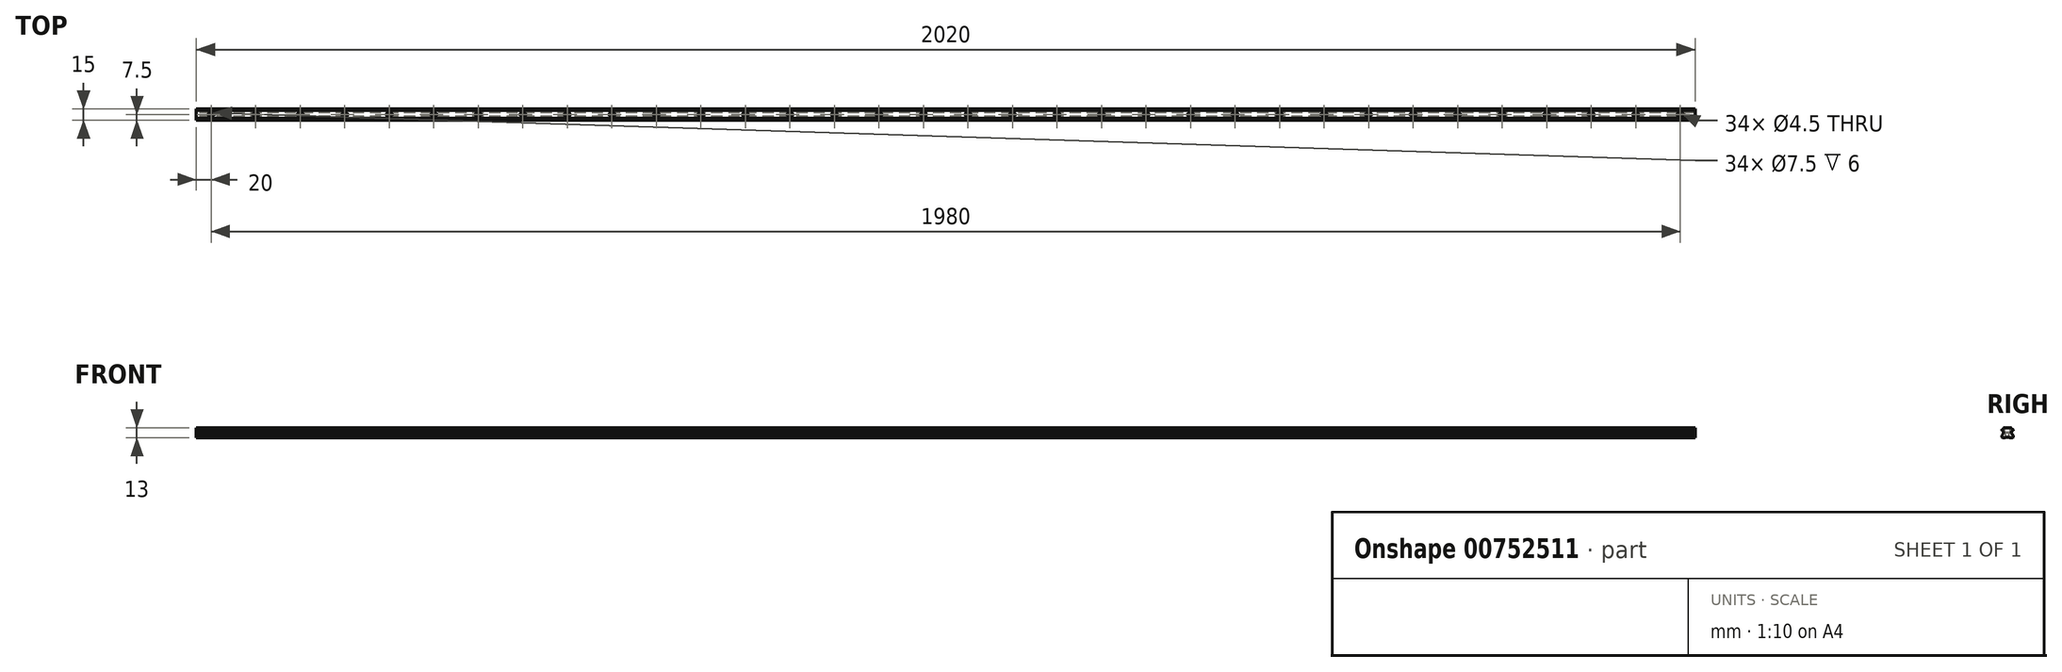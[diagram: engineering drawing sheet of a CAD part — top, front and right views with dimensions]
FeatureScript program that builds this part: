
annotation { "Feature Type Name" : "Feature", "Feature Type Description" : "" }
export const myFeature = defineFeature(function(context is Context, id is Id, definition is map)
    precondition{}
    {
        {
            var Q0;
            Q0=qCreatedBy(makeId("Right.planeOp"),FACE);
            var sketch = newSketch(context, id + "F0", { "sketchPlane" : qUnion([Q0])});
            skLineSegment(sketch, "E0", {"start": v(0, 0.5) * mm, "end": v(2.5, 0.5) * mm});
            skLineSegment(sketch, "E1", {"start": v(2.5, 0.5) * mm, "end": v(3, 0) * mm});
            skLineSegment(sketch, "E2", {"start": v(3, 0) * mm, "end": v(7, 0) * mm});
            skLineSegment(sketch, "E3", {"start": v(7, 0) * mm, "end": v(7.5, 0.5) * mm});
            skLineSegment(sketch, "E4", {"start": v(7.5, 0.5) * mm, "end": v(7.5, 3.3) * mm});
            skLineSegment(sketch, "E5", {"start": v(7.5, 3.3) * mm, "end": v(5.38, 5.42) * mm});
            skLineSegment(sketch, "E6", {"start": v(5.38, 5.42) * mm, "end": v(5.38, 7.26) * mm});
            skLineSegment(sketch, "E7", {"start": v(5.38, 7.26) * mm, "end": v(5.5, 7.38) * mm});
            skLineSegment(sketch, "E8", {"start": v(7.5, 9.38) * mm, "end": v(7.5, 10.88) * mm});
            skLineSegment(sketch, "E9", {"start": v(7.5, 10.88) * mm, "end": v(7.37, 11) * mm});
            skLineSegment(sketch, "E10", {"start": v(5.38, 13) * mm, "end": v(0, 13) * mm});
            skLineSegment(sketch, "E11", {"start": v(0, 13) * mm, "end": v(0, 0) * mm, "construction": true});
            skArc(sketch, "E12", {"start": v(5.5, 12.87) * mm, "mid": v(6.09, 11.59) * mm, "end": v(7.37, 11) * mm});
            skLineSegment(sketch, "E13", {"start": v(5.5, 12.87) * mm, "end": v(5.38, 13) * mm});
            skLineSegment(sketch, "E14", {"start": v(7.37, 11) * mm, "end": v(5.5, 12.87) * mm, "construction": true});
            skLineSegment(sketch, "E15", {"start": v(7.37, 9.25) * mm, "end": v(7.5, 9.38) * mm});
            skLineSegment(sketch, "E16", {"start": v(5.5, 7.38) * mm, "end": v(7.37, 9.25) * mm, "construction": true});
            skArc(sketch, "E17", {"start": v(7.37, 9.25) * mm, "mid": v(6.09, 8.67) * mm, "end": v(5.5, 7.38) * mm});
            skLineSegment(sketch, "E18.MirrorCS", {"start": v(-7.37, 9.25) * mm, "end": v(-7.5, 9.38) * mm});
            skLineSegment(sketch, "E19.MirrorCS", {"start": v(-5.5, 12.87) * mm, "end": v(-5.38, 13) * mm});
            skLineSegment(sketch, "E20.MirrorCS", {"start": v(-5.38, 7.26) * mm, "end": v(-5.5, 7.38) * mm});
            skLineSegment(sketch, "E21.MirrorCS", {"start": v(-7.5, 10.88) * mm, "end": v(-7.37, 11) * mm});
            skLineSegment(sketch, "E22.MirrorCS", {"start": v(-2.5, 0.5) * mm, "end": v(-3, 0) * mm});
            skLineSegment(sketch, "E23.MirrorCS", {"start": v(-7, 0) * mm, "end": v(-7.5, 0.5) * mm});
            skLineSegment(sketch, "E24.MirrorCS", {"start": v(-7.37, 11) * mm, "end": v(-5.5, 12.87) * mm, "construction": true});
            skLineSegment(sketch, "E25.MirrorCS", {"start": v(0, 0.5) * mm, "end": v(-2.5, 0.5) * mm});
            skLineSegment(sketch, "E26.MirrorCS", {"start": v(-5.5, 7.38) * mm, "end": v(-7.37, 9.25) * mm, "construction": true});
            skArc(sketch, "E27.MirrorCS", {"start": v(-7.37, 9.25) * mm, "mid": v(-6.09, 8.67) * mm, "end": v(-5.5, 7.38) * mm});
            skLineSegment(sketch, "E28.MirrorCS", {"start": v(-5.38, 13) * mm, "end": v(0, 13) * mm});
            skArc(sketch, "E29.MirrorCS", {"start": v(-5.5, 12.87) * mm, "mid": v(-6.09, 11.59) * mm, "end": v(-7.37, 11) * mm});
            skLineSegment(sketch, "E30.MirrorCS", {"start": v(-7.5, 0.5) * mm, "end": v(-7.5, 3.3) * mm});
            skLineSegment(sketch, "E31.MirrorCS", {"start": v(-7.5, 3.3) * mm, "end": v(-5.38, 5.42) * mm});
            skLineSegment(sketch, "E32.MirrorCS", {"start": v(-7.5, 9.38) * mm, "end": v(-7.5, 10.88) * mm});
            skLineSegment(sketch, "E33.MirrorCS", {"start": v(-3, 0) * mm, "end": v(-7, 0) * mm});
            skLineSegment(sketch, "E34.MirrorCS", {"start": v(-5.38, 5.42) * mm, "end": v(-5.38, 7.26) * mm});
            skSolve(sketch);
        }
        {
            var Q0;
            Q0=qSketchRegion(id+"F0",true);
            extrude(context, id + "F1", {"entities" : qUnion([Q0]), "depth" : 2020 * mm, "offsetDistance" : 25 * mm});
        }
        {
            var Q0;
            Q0=makeQuery(id+"F1.opExtrude","SWEPT_FACE",FACE,{"disambiguationData":[OSD([sQuery(id+"F0.wireOp",EDGE,"E10"),sQuery(id+"F0.wireOp",EDGE,"E28.MirrorCS")])]});
            var sketch = newSketch(context, id + "F2", { "sketchPlane" : qUnion([Q0])});
            skPoint(sketch, "E35", {"position": v(20, 0) * mm});
            skPoint(sketch, "E36.1.0.0", {"position": v(80, 0) * mm});
            skPoint(sketch, "E36.2.0.0", {"position": v(140, 0) * mm});
            skPoint(sketch, "E36.3.0.0", {"position": v(200, 0) * mm});
            skPoint(sketch, "E36.4.0.0", {"position": v(260, 0) * mm});
            skPoint(sketch, "E36.5.0.0", {"position": v(320, 0) * mm});
            skPoint(sketch, "E36.6.0.0", {"position": v(380, 0) * mm});
            skPoint(sketch, "E36.7.0.0", {"position": v(440, 0) * mm});
            skPoint(sketch, "E36.8.0.0", {"position": v(500, 0) * mm});
            skPoint(sketch, "E36.9.0.0", {"position": v(560, 0) * mm});
            skPoint(sketch, "E36.10.0.0", {"position": v(620, 0) * mm});
            skPoint(sketch, "E36.11.0.0", {"position": v(680, 0) * mm});
            skPoint(sketch, "E36.12.0.0", {"position": v(740, 0) * mm});
            skPoint(sketch, "E36.13.0.0", {"position": v(800, 0) * mm});
            skPoint(sketch, "E36.14.0.0", {"position": v(860, 0) * mm});
            skPoint(sketch, "E36.15.0.0", {"position": v(920, 0) * mm});
            skPoint(sketch, "E36.16.0.0", {"position": v(980, 0) * mm});
            skPoint(sketch, "E36.17.0.0", {"position": v(1040, 0) * mm});
            skPoint(sketch, "E36.18.0.0", {"position": v(1100, 0) * mm});
            skPoint(sketch, "E36.19.0.0", {"position": v(1160, 0) * mm});
            skPoint(sketch, "E36.20.0.0", {"position": v(1220, 0) * mm});
            skPoint(sketch, "E36.21.0.0", {"position": v(1280, 0) * mm});
            skPoint(sketch, "E36.22.0.0", {"position": v(1340, 0) * mm});
            skPoint(sketch, "E36.23.0.0", {"position": v(1400, 0) * mm});
            skPoint(sketch, "E36.24.0.0", {"position": v(1460, 0) * mm});
            skPoint(sketch, "E36.25.0.0", {"position": v(1520, 0) * mm});
            skPoint(sketch, "E36.26.0.0", {"position": v(1580, 0) * mm});
            skPoint(sketch, "E36.27.0.0", {"position": v(1640, 0) * mm});
            skPoint(sketch, "E36.28.0.0", {"position": v(1700, 0) * mm});
            skPoint(sketch, "E36.29.0.0", {"position": v(1760, 0) * mm});
            skLineSegment(sketch, "E36.direction1", {"start": v(20, 0) * mm, "end": v(80, 0) * mm, "construction": true});
            skPoint(sketch, "E37.0.30.0", {"position": v(1820, 0) * mm});
            skPoint(sketch, "E37.0.31.0", {"position": v(1880, 0) * mm});
            skPoint(sketch, "E37.0.32.0", {"position": v(1940, 0) * mm});
            skPoint(sketch, "E37.0.33.0", {"position": v(2000, 0) * mm});
            skPoint(sketch, "E37.0.34.0", {"position": v(2060, 0) * mm});
            skPoint(sketch, "E37.0.35.0", {"position": v(2120, 0) * mm});
            skPoint(sketch, "E37.0.36.0", {"position": v(2180, 0) * mm});
            skPoint(sketch, "E37.0.37.0", {"position": v(2240, 0) * mm});
            skPoint(sketch, "E37.0.38.0", {"position": v(2300, 0) * mm});
            skPoint(sketch, "E37.0.39.0", {"position": v(2360, 0) * mm});
            skSolve(sketch);
        }
        {
            var Q0;
            Q0=sQuery(id+"F2.wireOp",VERTEX,"E35");
            var Q1;
            Q1=sQuery(id+"F2.wireOp",VERTEX,"E36.1.0.0");
            var Q2;
            Q2=sQuery(id+"F2.wireOp",VERTEX,"E36.2.0.0");
            var Q3;
            Q3=sQuery(id+"F2.wireOp",VERTEX,"E36.3.0.0");
            var Q4;
            Q4=sQuery(id+"F2.wireOp",VERTEX,"E36.4.0.0");
            var Q5;
            Q5=sQuery(id+"F2.wireOp",VERTEX,"E36.5.0.0");
            var Q6;
            Q6=sQuery(id+"F2.wireOp",VERTEX,"E36.6.0.0");
            var Q7;
            Q7=sQuery(id+"F2.wireOp",VERTEX,"E36.7.0.0");
            var Q8;
            Q8=sQuery(id+"F2.wireOp",VERTEX,"E36.8.0.0");
            var Q9;
            Q9=sQuery(id+"F2.wireOp",VERTEX,"E36.9.0.0");
            var Q10;
            Q10=sQuery(id+"F2.wireOp",VERTEX,"E36.10.0.0");
            var Q11;
            Q11=sQuery(id+"F2.wireOp",VERTEX,"E36.11.0.0");
            var Q12;
            Q12=sQuery(id+"F2.wireOp",VERTEX,"E36.12.0.0");
            var Q13;
            Q13=sQuery(id+"F2.wireOp",VERTEX,"E36.13.0.0");
            var Q14;
            Q14=sQuery(id+"F2.wireOp",VERTEX,"E36.14.0.0");
            var Q15;
            Q15=sQuery(id+"F2.wireOp",VERTEX,"E36.15.0.0");
            var Q16;
            Q16=sQuery(id+"F2.wireOp",VERTEX,"E36.16.0.0");
            var Q17;
            Q17=sQuery(id+"F2.wireOp",VERTEX,"E36.17.0.0");
            var Q18;
            Q18=sQuery(id+"F2.wireOp",VERTEX,"E36.18.0.0");
            var Q19;
            Q19=sQuery(id+"F2.wireOp",VERTEX,"E36.19.0.0");
            var Q20;
            Q20=sQuery(id+"F2.wireOp",VERTEX,"E36.20.0.0");
            var Q21;
            Q21=sQuery(id+"F2.wireOp",VERTEX,"E36.21.0.0");
            var Q22;
            Q22=sQuery(id+"F2.wireOp",VERTEX,"E36.22.0.0");
            var Q23;
            Q23=sQuery(id+"F2.wireOp",VERTEX,"E36.23.0.0");
            var Q24;
            Q24=sQuery(id+"F2.wireOp",VERTEX,"E36.24.0.0");
            var Q25;
            Q25=sQuery(id+"F2.wireOp",VERTEX,"E36.25.0.0");
            var Q26;
            Q26=sQuery(id+"F2.wireOp",VERTEX,"E36.26.0.0");
            var Q27;
            Q27=sQuery(id+"F2.wireOp",VERTEX,"E36.27.0.0");
            var Q28;
            Q28=sQuery(id+"F2.wireOp",VERTEX,"E36.28.0.0");
            var Q29;
            Q29=sQuery(id+"F2.wireOp",VERTEX,"E36.29.0.0");
            var Q30;
            Q30=sQuery(id+"F2.wireOp",VERTEX,"E37.0.30.0");
            var Q31;
            Q31=sQuery(id+"F2.wireOp",VERTEX,"E37.0.31.0");
            var Q32;
            Q32=sQuery(id+"F2.wireOp",VERTEX,"E37.0.32.0");
            var Q33;
            Q33=sQuery(id+"F2.wireOp",VERTEX,"E37.0.33.0");
            var Q34;
            Q34=makeQuery(id+"F1.opExtrude","SWEPT_BODY",BODY,{"disambiguationData":[OSD([sQuery(id+"F0.wireOp",EDGE,"E0"),sQuery(id+"F0.wireOp",EDGE,"E1"),sQuery(id+"F0.wireOp",EDGE,"E2"),sQuery(id+"F0.wireOp",EDGE,"E3"),sQuery(id+"F0.wireOp",EDGE,"E4"),sQuery(id+"F0.wireOp",EDGE,"E5"),sQuery(id+"F0.wireOp",EDGE,"E6"),sQuery(id+"F0.wireOp",EDGE,"E7"),sQuery(id+"F0.wireOp",EDGE,"E8"),sQuery(id+"F0.wireOp",EDGE,"E9"),sQuery(id+"F0.wireOp",EDGE,"E10"),sQuery(id+"F0.wireOp",EDGE,"E12"),sQuery(id+"F0.wireOp",EDGE,"E13"),sQuery(id+"F0.wireOp",EDGE,"E15"),sQuery(id+"F0.wireOp",EDGE,"E17"),sQuery(id+"F0.wireOp",EDGE,"E18.MirrorCS"),sQuery(id+"F0.wireOp",EDGE,"E19.MirrorCS"),sQuery(id+"F0.wireOp",EDGE,"E20.MirrorCS"),sQuery(id+"F0.wireOp",EDGE,"E21.MirrorCS"),sQuery(id+"F0.wireOp",EDGE,"E22.MirrorCS"),sQuery(id+"F0.wireOp",EDGE,"E23.MirrorCS"),sQuery(id+"F0.wireOp",EDGE,"E25.MirrorCS"),sQuery(id+"F0.wireOp",EDGE,"E27.MirrorCS"),sQuery(id+"F0.wireOp",EDGE,"E28.MirrorCS"),sQuery(id+"F0.wireOp",EDGE,"E29.MirrorCS"),sQuery(id+"F0.wireOp",EDGE,"E30.MirrorCS"),sQuery(id+"F0.wireOp",EDGE,"E31.MirrorCS"),sQuery(id+"F0.wireOp",EDGE,"E32.MirrorCS"),sQuery(id+"F0.wireOp",EDGE,"E33.MirrorCS"),sQuery(id+"F0.wireOp",EDGE,"E34.MirrorCS")])]});
            hole(context, id + "F3", {"style" : HoleStyle.C_BORE, "endStyle" : HoleEndStyle.THROUGH, "holeDiameter" : 4.5 * mm, "cBoreDiameter" : 7.5 * mm, "cBoreDepth" : 6 * mm, "majorDiameter" : 5 * mm, "isTappedThrough" : true, "tappedDepth" : 12 * mm, "tapClearance" : 3, "startFromSketch" : true, "locations" : qUnion([Q0, Q1, Q2, Q3, Q4, Q5, Q6, Q7, Q8, Q9, Q10, Q11, Q12, Q13, Q14, Q15, Q16, Q17, Q18, Q19, Q20, Q21, Q22, Q23, Q24, Q25, Q26, Q27, Q28, Q29, Q30, Q31, Q32, Q33]), "scope" : qUnion([Q34])});
        }
    });
